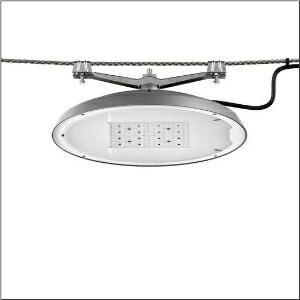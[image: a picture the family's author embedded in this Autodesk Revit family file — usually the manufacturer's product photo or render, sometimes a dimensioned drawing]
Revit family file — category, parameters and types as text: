
# Revit family: dl_r__50_iq_mini___st1_0s_5xa248w21f08le_63d0
name_source: partatom
category: Lighting Fixtures
units: mm (PartAtom-declared; Revit-internal decimal feet)

## family parameters
Cut with Voids When Loaded = No
Host = Face
Light Source = No
Part Type = Normal
Room Calculation Point = No
Round Connector Dimension = Use Diameter
Shared = No

## types (1)
- --- (1 x LED, 8560 lm, 66.9 W, 2200K)
    Apparent Load = 67 VA
    CIE Flux Codes = 37 72 97 100 100
    Color Rendering = 70
    Color Temperature = 2200K
    Default Elevation = 1800 mm
    Description = DL® 50 iQ mini, catenary luminaire, primary light control with lens, of PMMA, primary optical cover: cover, of toughened safety glass, transparent, light distribution: ST1.0s, light emission: direct distribution, primary light characteristic: symmetric, installation type: suspended mounting, LED, High Power LED, rated luminous flux: 8.560lm, luminous efficacy: 128lm/W, light colour: 722, colour temperature: 2200K, control gear: iQ Street-Remote, control: optimised constant luminous flux control (CLO 2.0), Desk-Remote (wireless, voltage-free reading and setting of iQ features in the workshop via application-optimized NFC function/RFID function), Light-Fading, Smart-Wire, Night-Set, Lumen-Switch, Temp-Guard, Auto-Match, Street-Remote, mains connection: 230..240V, AC, 50/60Hz, start of lifetime: 67W, end of service life: 70W, reduction: 31W, luminaire housing, of diecast aluminium, powder-coated, Siteco® metallic grey (DB 702S), diameter: 500mm, height: 115mm, mounting height: 4..12m, protection rating (complete): IP66, insulation class (complete): insulation class II (safety insulation), certification: CE, ENEC, ENEC+, VDE, impact resistance: IK08, permissible operating ambient temperature for outdoor applications: -25..+40°C, standard-compliant lighting for roads and squares, packaging unit: 1 piece

Light Distribution: ST1.0s
    Height = 124 mm  [stored 0.406824 ft]
    Lamp = 1 x LED
    Lamp Light Flux = 8560 lm
    Lamp Power = 66.9 W
    Lamp count = 1
    Length = 500 mm
    Luminous efficacy = 128 lm/W
    Manufacturer = Siteco
    ModVariant = No
    Model = 5XA248W21F08LE
    Number of Poles = 1
    OnlyDefault = Yes
    Power Factor = 1
    Product Name = DL® 50 iQ mini | ST1.0s
    Product group = catenary luminaire
    ProductGroupID = 6300
    Protection Class = Protection class II
    Protection Degree = IP 66
    RLX_Detail_Level = 1
    RLX_Emergency_Light_Flux = 0 lm
    RLX_Emergency_Type = 0
    RLX_Emergency_Type_DB = No
    RlxData = <blob elided: 127141 chars, md5=7ba89753>
    Socket = socket
    Standby Power = 0 W
    System Light Flux = 8560 lm
    System Power = 67 W
    Type Comments = factory setting: luminous flux: 100 % | dim-lin: 254 | 700 mA
    Type Image = l_1251783.jpg
    URL = http://relux.com
    VarID = @adj_162043
    Voltage = 0 V
    Weight = 0.00 kg
    Width = 0 mm  [stored 0 ft]

note: [stored X ft] marks values corroborated as IEEE doubles in the binary element streams (Revit-internal decimal feet)

## geometry (parser evidence)
native form markers: Blend x4, Sweep x13
no freeform markers — native parametric forms only
